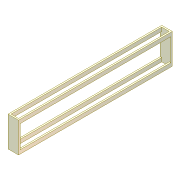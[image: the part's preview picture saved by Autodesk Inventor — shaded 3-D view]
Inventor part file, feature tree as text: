
AUTODESK INVENTOR PART (.ipt)
format: ipt  version: unknown  size: 197,120 bytes
history: native  units: in
note: dims shown in document units (in); Inventor stores cm internally (conversion verified against a paired STEP export)
features: extrude x2, sketch x2, mirror x1, projected_geometry x1
ambient origin geometry x8: Origin, YZ Plane, XZ Plane, XY Plane, X Axis, Y Axis, Z Axis, Center Point
feature tree (6):
  extrude  "Extrusion44"  Depth=0.0787in
  extrude  "Extrusion45"  Depth=0.1969in
  mirror  "Mirror3"
  sketch  "Sketch44"  dims[d207=0.2756in d208=0.0787in]
  sketch  "Sketch45"  dims[d209=0.5906in d210=0.1969in d211=7.874in d212=0.0in d213=0.0787in d214=0.0in]
  projected_geometry  "Projected Loop2"
